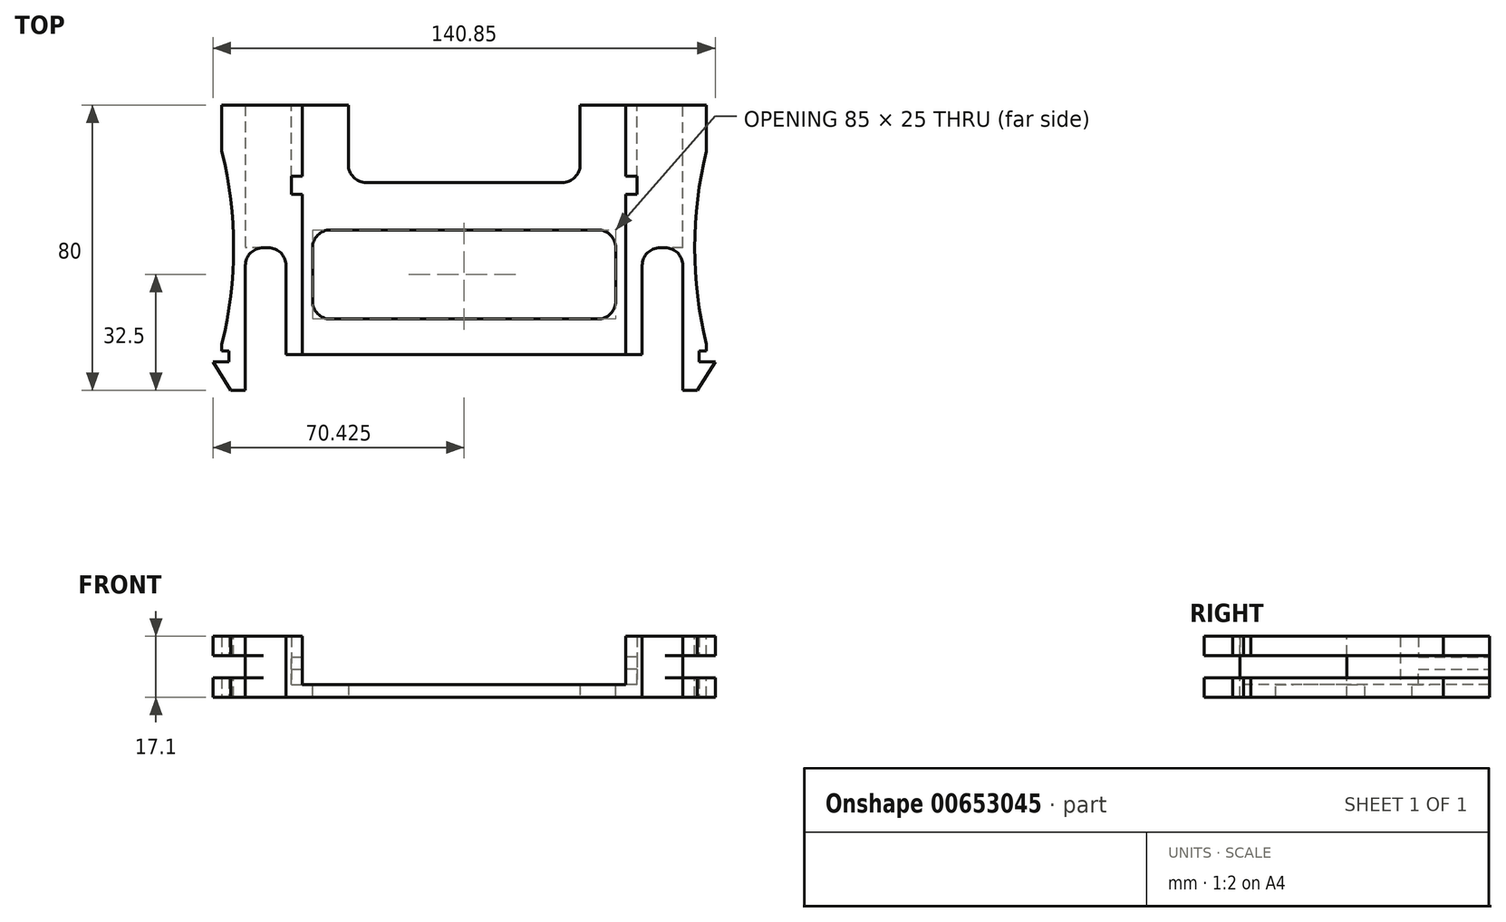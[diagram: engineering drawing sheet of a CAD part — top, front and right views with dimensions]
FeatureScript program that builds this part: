
annotation { "Feature Type Name" : "Feature", "Feature Type Description" : "" }
export const myFeature = defineFeature(function(context is Context, id is Id, definition is map)
    precondition{}
    {
        {
            var Q0;
            Q0=qCreatedBy(makeId("Top.planeOp"),FACE);
            var sketch = newSketch(context, id + "F0", { "sketchPlane" : qUnion([Q0])});
            skLineSegment(sketch, "E0.bottom", {"start": v(0, 0) * mm, "end": v(100.65, 0) * mm});
            skLineSegment(sketch, "E0.top", {"start": v(0, 134.5) * mm, "end": v(100.65, 134.5) * mm});
            skLineSegment(sketch, "E0.left", {"start": v(0, 0) * mm, "end": v(0, 134.5) * mm});
            skLineSegment(sketch, "E0.right", {"start": v(100.65, 0) * mm, "end": v(100.65, 134.5) * mm});
            skSolve(sketch);
        }
        {
            var Q0;
            Q0=makeQuery(id+"F0.imprint","IMPRINT",FACE,{"disambiguationData":[TD([[makeQuery(id+"F0.imprint","IMPRINT",EDGE,{"derivedFrom":sQuery(id+"F0.wireOp",EDGE,"E0.bottom")}),1.0]])]});
            extrude(context, id + "F1", {"entities" : qUnion([Q0]), "depth" : 2 * mm, "offsetDistance" : 25 * mm});
        }
        {
            var Q0;
            Q0=makeQuery(id+"F1.opExtrude","CAP_FACE",FACE,{"disambiguationData":[OSD([sQuery(id+"F0.wireOp",EDGE,"E0.bottom"),sQuery(id+"F0.wireOp",EDGE,"E0.top"),sQuery(id+"F0.wireOp",EDGE,"E0.left"),sQuery(id+"F0.wireOp",EDGE,"E0.right")])],"isStart":false});
            var sketch = newSketch(context, id + "F2", { "sketchPlane" : qUnion([Q0])});
            skLineSegment(sketch, "E1.bottom", {"start": v(0, 134.5) * mm, "end": v(5, 134.5) * mm});
            skLineSegment(sketch, "E1.top", {"start": v(0, 0) * mm, "end": v(5, 0) * mm});
            skLineSegment(sketch, "E1.left", {"start": v(0, 134.5) * mm, "end": v(0, 0) * mm});
            skLineSegment(sketch, "E1.right", {"start": v(5, 134.5) * mm, "end": v(5, 0) * mm});
            skLineSegment(sketch, "E2.bottom", {"start": v(100.65, 134.5) * mm, "end": v(95.65, 134.5) * mm});
            skLineSegment(sketch, "E2.top", {"start": v(100.65, 0) * mm, "end": v(95.65, 0) * mm});
            skLineSegment(sketch, "E2.left", {"start": v(100.65, 134.5) * mm, "end": v(100.65, 0) * mm});
            skLineSegment(sketch, "E2.right", {"start": v(95.65, 134.5) * mm, "end": v(95.65, 0) * mm});
            skSolve(sketch);
        }
        {
            var Q0;
            Q0=makeQuery(id+"F2.imprint","IMPRINT",FACE,{"disambiguationData":[TD([[makeQuery(id+"F2.imprint","IMPRINT",EDGE,{"derivedFrom":sQuery(id+"F2.wireOp",EDGE,"E1.bottom")}),-1.0]])]});
            var Q1;
            Q1=makeQuery(id+"F2.imprint","IMPRINT",FACE,{"disambiguationData":[TD([[makeQuery(id+"F2.imprint","IMPRINT",EDGE,{"derivedFrom":sQuery(id+"F2.wireOp",EDGE,"E2.bottom")}),-1.0]])]});
            extrude(context, id + "F3", {"entities" : qUnion([Q0, Q1]), "operationType" : NewBodyOperationType.ADD, "depth" : 11.9 * mm, "offsetDistance" : 25 * mm});
        }
        {
            var Q0;
            Q0=makeQuery(id+"F3.boolean.opBoolean","MERGE",FACE,{"derivedFrom":[makeQuery(id+"F1.opExtrude","SWEPT_FACE",FACE,{"disambiguationData":[OSD([sQuery(id+"F0.wireOp",EDGE,"E0.top")])]}),makeQuery(id+"F3.opExtrude","SWEPT_FACE",FACE,{"disambiguationData":[OSD([sQuery(id+"F2.wireOp",EDGE,"E1.bottom")])]}),makeQuery(id+"F3.opExtrude","SWEPT_FACE",FACE,{"disambiguationData":[OSD([sQuery(id+"F2.wireOp",EDGE,"E2.bottom")])]})]});
            var sketch = newSketch(context, id + "F4", { "sketchPlane" : qUnion([Q0])});
            skLineSegment(sketch, "E3.bottom", {"start": v(-100.65, 13.9) * mm, "end": v(-95.65, 13.9) * mm});
            skLineSegment(sketch, "E3.top", {"start": v(-100.65, 0) * mm, "end": v(-95.65, 0) * mm});
            skLineSegment(sketch, "E3.left", {"start": v(-100.65, 13.9) * mm, "end": v(-100.65, 0) * mm});
            skLineSegment(sketch, "E3.right", {"start": v(-95.65, 13.9) * mm, "end": v(-95.65, 0) * mm});
            skLineSegment(sketch, "E4.bottom", {"start": v(0, 13.9) * mm, "end": v(-5, 13.9) * mm});
            skLineSegment(sketch, "E4.top", {"start": v(0, 0) * mm, "end": v(-5, 0) * mm});
            skLineSegment(sketch, "E4.left", {"start": v(0, 13.9) * mm, "end": v(0, 0) * mm});
            skLineSegment(sketch, "E4.right", {"start": v(-5, 13.9) * mm, "end": v(-5, 0) * mm});
            skSolve(sketch);
        }
        {
            var Q0;
            {var subQ1=sQuery(id+"F4.wireOp",EDGE,"E3.bottom");Q0=makeQuery(id+"F4.imprint","IMPRINT",FACE,{"disambiguationData":[TD([[makeQuery(id+"F4.imprint","IMPRINT",EDGE,{"derivedFrom":subQ1}),1.0]])]});}
            var Q1;
            {var subQ1=sQuery(id+"F4.wireOp",EDGE,"E4.bottom");Q1=makeQuery(id+"F4.imprint","IMPRINT",FACE,{"disambiguationData":[TD([[makeQuery(id+"F4.imprint","IMPRINT",EDGE,{"derivedFrom":subQ1}),1.0]])]});}
            extrude(context, id + "F5", {"entities" : qUnion([Q0, Q1]), "operationType" : NewBodyOperationType.ADD, "depth" : 45 * mm, "offsetDistance" : 25 * mm});
        }
        {
            var Q0;
            Q0=makeQuery(id+"F5.boolean.opBoolean","MERGE",FACE,{"derivedFrom":[makeQuery(id+"F3.opExtrude","SWEPT_FACE",FACE,{"disambiguationData":[OSD([sQuery(id+"F2.wireOp",EDGE,"E1.right")])]}),makeQuery(id+"F5.opExtrude","SWEPT_FACE",FACE,{"disambiguationData":[OSD([sQuery(id+"F4.wireOp",EDGE,"E4.right")])]})]});
            var sketch = newSketch(context, id + "F6", { "sketchPlane" : qUnion([Q0])});
            skLineSegment(sketch, "E5", {"start": v(45, 13.9) * mm, "end": v(45, 2) * mm});
            skLineSegment(sketch, "E6", {"start": v(134.5, 2) * mm, "end": v(134.5, 4.2) * mm});
            skLineSegment(sketch, "E7", {"start": v(50, 2) * mm, "end": v(50, 6.2) * mm});
            skLineSegment(sketch, "E8", {"start": v(50, 6.2) * mm, "end": v(70, 6.2) * mm});
            skLineSegment(sketch, "E9", {"start": v(70, 6.2) * mm, "end": v(134.5, 2) * mm});
            skLineSegment(sketch, "E10", {"start": v(134.5, 9.7) * mm, "end": v(179.5, 9.7) * mm});
            skLineSegment(sketch, "E11", {"start": v(134.5, 4.2) * mm, "end": v(179.5, 4.2) * mm});
            skLineSegment(sketch, "E12.trimOffspring", {"start": v(134.5, 9.7) * mm, "end": v(134.5, 13.9) * mm});
            skLineSegment(sketch, "E13", {"start": v(50, 13.9) * mm, "end": v(50, 9.7) * mm});
            skLineSegment(sketch, "E14", {"start": v(50, 9.7) * mm, "end": v(70, 9.7) * mm});
            skLineSegment(sketch, "E15", {"start": v(70, 9.7) * mm, "end": v(70, 13.9) * mm});
            skSolve(sketch);
        }
        {
            var Q0;
            Q0=makeQuery(id+"F5.boolean.opBoolean","MERGE",FACE,{"derivedFrom":[makeQuery(id+"F3.opExtrude","SWEPT_FACE",FACE,{"disambiguationData":[OSD([sQuery(id+"F2.wireOp",EDGE,"E2.right")])]}),makeQuery(id+"F5.opExtrude","SWEPT_FACE",FACE,{"disambiguationData":[OSD([sQuery(id+"F4.wireOp",EDGE,"E3.right")])]})]});
            var sketch = newSketch(context, id + "F7", { "sketchPlane" : qUnion([Q0])});
            skLineSegment(sketch, "E16", {"start": v(-45, 13.9) * mm, "end": v(-45, 2) * mm});
            skLineSegment(sketch, "E17", {"start": v(-134.5, 13.9) * mm, "end": v(-134.5, 9.7) * mm});
            skLineSegment(sketch, "E18", {"start": v(-50, 2) * mm, "end": v(-50, 6.2) * mm});
            skLineSegment(sketch, "E19", {"start": v(-50, 6.2) * mm, "end": v(-70, 6.2) * mm});
            skLineSegment(sketch, "E20", {"start": v(-70, 6.2) * mm, "end": v(-134.5, 2) * mm});
            skLineSegment(sketch, "E21", {"start": v(-179.5, 4.2) * mm, "end": v(-134.5, 4.2) * mm});
            skLineSegment(sketch, "E22", {"start": v(-179.5, 9.7) * mm, "end": v(-134.5, 9.7) * mm});
            skLineSegment(sketch, "E23.trimOffspring", {"start": v(-134.5, 4.2) * mm, "end": v(-134.5, 2) * mm});
            skLineSegment(sketch, "E24", {"start": v(-50, 13.9) * mm, "end": v(-50, 9.7) * mm});
            skLineSegment(sketch, "E25", {"start": v(-50, 9.7) * mm, "end": v(-70, 9.7) * mm});
            skLineSegment(sketch, "E26", {"start": v(-70, 9.7) * mm, "end": v(-70, 13.9) * mm});
            skSolve(sketch);
        }
        {
            var Q0;
            {var subQ0=sQuery(id+"F7.wireOp",EDGE,"E16");Q0=makeQuery(id+"F7.imprint","IMPRINT",FACE,{"disambiguationData":[TD([[makeQuery(id+"F7.imprint","IMPRINT",EDGE,{"derivedFrom":subQ0}),-1.0]])]});}
            extrude(context, id + "F8", {"entities" : qUnion([Q0]), "operationType" : NewBodyOperationType.REMOVE, "oppositeDirection" : true, "depth" : 3.1 * mm, "offsetDistance" : 25 * mm});
        }
        {
            var Q0;
            {var subQ3=sQuery(id+"F6.wireOp",EDGE,"E5");Q0=makeQuery(id+"F6.imprint","IMPRINT",FACE,{"disambiguationData":[TD([[makeQuery(id+"F6.imprint","IMPRINT",EDGE,{"derivedFrom":subQ3}),1.0]])]});}
            extrude(context, id + "F9", {"entities" : qUnion([Q0]), "operationType" : NewBodyOperationType.REMOVE, "oppositeDirection" : true, "depth" : 3.1 * mm, "offsetDistance" : 25 * mm});
        }
        {
            var Q0;
            Q0=makeQuery(id+"F9.boolean.opBoolean","MERGE",FACE,{"derivedFrom":[makeQuery(id+"F8.boolean.opBoolean","MERGE",FACE,{"derivedFrom":[makeQuery(id+"F1.opExtrude","CAP_FACE",FACE,{"disambiguationData":[OSD([sQuery(id+"F0.wireOp",EDGE,"E0.bottom"),sQuery(id+"F0.wireOp",EDGE,"E0.top"),sQuery(id+"F0.wireOp",EDGE,"E0.left"),sQuery(id+"F0.wireOp",EDGE,"E0.right")])],"isStart":false}),makeQuery(id+"F8.opExtrude","SWEPT_FACE",FACE,{"disambiguationData":[OSD([sQuery(id+"F2.wireOp",EDGE,"E2.right")])]})]}),makeQuery(id+"F9.opExtrude","SWEPT_FACE",FACE,{"disambiguationData":[OSD([sQuery(id+"F2.wireOp",EDGE,"E1.right")])]})]});
            var sketch = newSketch(context, id + "F10", { "sketchPlane" : qUnion([Q0])});
            skLineSegment(sketch, "E27.bottom", {"start": v(12.83, 35) * mm, "end": v(87.82, 35) * mm});
            skLineSegment(sketch, "E27.top", {"start": v(12.83, 10) * mm, "end": v(87.82, 10) * mm});
            skLineSegment(sketch, "E27.left", {"start": v(7.83, 30) * mm, "end": v(7.83, 15) * mm});
            skLineSegment(sketch, "E27.right", {"start": v(92.83, 30) * mm, "end": v(92.83, 15) * mm});
            skLineSegment(sketch, "E28.bottom", {"start": v(22.85, 83.32) * mm, "end": v(77.85, 83.32) * mm});
            skLineSegment(sketch, "E28.top", {"start": v(22.85, 48.32) * mm, "end": v(77.85, 48.32) * mm});
            skLineSegment(sketch, "E28.left", {"start": v(17.85, 78.32) * mm, "end": v(17.85, 53.32) * mm});
            skLineSegment(sketch, "E28.right", {"start": v(82.85, 78.32) * mm, "end": v(82.85, 53.32) * mm});
            skLineSegment(sketch, "E29.bottom", {"start": v(22.85, 127.47) * mm, "end": v(77.85, 127.47) * mm});
            skLineSegment(sketch, "E29.top", {"start": v(22.85, 92.47) * mm, "end": v(77.85, 92.47) * mm});
            skLineSegment(sketch, "E29.left", {"start": v(17.85, 122.47) * mm, "end": v(17.85, 97.47) * mm});
            skLineSegment(sketch, "E29.right", {"start": v(82.85, 122.47) * mm, "end": v(82.85, 97.47) * mm});
            skPoint(sketch, "E30.visualSharp", {"position": v(17.85, 127.47) * mm});
            skArc(sketch, "E30.filletArc", {"start": v(22.85, 127.47) * mm, "mid": v(19.31, 126) * mm, "end": v(17.85, 122.47) * mm});
            skPoint(sketch, "E31.visualSharp", {"position": v(82.85, 127.47) * mm});
            skArc(sketch, "E31.filletArc", {"start": v(82.85, 122.47) * mm, "mid": v(81.39, 126) * mm, "end": v(77.85, 127.47) * mm});
            skPoint(sketch, "E32.visualSharp", {"position": v(82.85, 92.47) * mm});
            skArc(sketch, "E32.filletArc", {"start": v(77.85, 92.47) * mm, "mid": v(81.39, 93.93) * mm, "end": v(82.85, 97.47) * mm});
            skPoint(sketch, "E33.visualSharp", {"position": v(17.85, 92.47) * mm});
            skArc(sketch, "E33.filletArc", {"start": v(17.85, 97.47) * mm, "mid": v(19.31, 93.93) * mm, "end": v(22.85, 92.47) * mm});
            skPoint(sketch, "E34.visualSharp", {"position": v(17.85, 83.32) * mm});
            skArc(sketch, "E34.filletArc", {"start": v(22.85, 83.32) * mm, "mid": v(19.31, 81.85) * mm, "end": v(17.85, 78.32) * mm});
            skPoint(sketch, "E35.visualSharp", {"position": v(82.85, 83.32) * mm});
            skArc(sketch, "E35.filletArc", {"start": v(82.85, 78.32) * mm, "mid": v(81.39, 81.85) * mm, "end": v(77.85, 83.32) * mm});
            skPoint(sketch, "E36.visualSharp", {"position": v(82.85, 48.32) * mm});
            skArc(sketch, "E36.filletArc", {"start": v(77.85, 48.32) * mm, "mid": v(81.39, 49.78) * mm, "end": v(82.85, 53.32) * mm});
            skPoint(sketch, "E37.visualSharp", {"position": v(17.85, 48.32) * mm});
            skArc(sketch, "E37.filletArc", {"start": v(17.85, 53.32) * mm, "mid": v(19.31, 49.78) * mm, "end": v(22.85, 48.32) * mm});
            skPoint(sketch, "E38.visualSharp", {"position": v(7.83, 35) * mm});
            skArc(sketch, "E38.filletArc", {"start": v(12.83, 35) * mm, "mid": v(9.29, 33.54) * mm, "end": v(7.83, 30) * mm});
            skPoint(sketch, "E39.visualSharp", {"position": v(92.83, 35) * mm});
            skArc(sketch, "E39.filletArc", {"start": v(92.83, 30) * mm, "mid": v(91.36, 33.54) * mm, "end": v(87.82, 35) * mm});
            skPoint(sketch, "E40.visualSharp", {"position": v(92.83, 10) * mm});
            skArc(sketch, "E40.filletArc", {"start": v(87.82, 10) * mm, "mid": v(91.36, 11.46) * mm, "end": v(92.83, 15) * mm});
            skPoint(sketch, "E41.visualSharp", {"position": v(7.83, 10) * mm});
            skArc(sketch, "E41.filletArc", {"start": v(7.83, 15) * mm, "mid": v(9.29, 11.46) * mm, "end": v(12.83, 10) * mm});
            skSolve(sketch);
        }
        {
            var Q0;
            Q0=makeQuery(id+"F10.imprint","IMPRINT",FACE,{"disambiguationData":[TD([[makeQuery(id+"F10.imprint","IMPRINT",EDGE,{"derivedFrom":sQuery(id+"F10.wireOp",EDGE,"E29.bottom")}),-1.0]])]});
            var Q1;
            Q1=makeQuery(id+"F10.imprint","IMPRINT",FACE,{"disambiguationData":[TD([[makeQuery(id+"F10.imprint","IMPRINT",EDGE,{"derivedFrom":sQuery(id+"F10.wireOp",EDGE,"E28.bottom")}),-1.0]])]});
            var Q2;
            Q2=makeQuery(id+"F10.imprint","IMPRINT",FACE,{"disambiguationData":[TD([[makeQuery(id+"F10.imprint","IMPRINT",EDGE,{"derivedFrom":sQuery(id+"F10.wireOp",EDGE,"E27.bottom")}),-1.0]])]});
            extrude(context, id + "F11", {"entities" : qUnion([Q0, Q1, Q2]), "operationType" : NewBodyOperationType.REMOVE, "oppositeDirection" : true, "depth" : 2 * mm, "offsetDistance" : 25 * mm});
        }
        {
            var Q0;
            Q0=makeQuery(id+"F5.boolean.opBoolean","MERGE",FACE,{"derivedFrom":[makeQuery(id+"F3.opExtrude","CAP_FACE",FACE,{"disambiguationData":[OSD([sQuery(id+"F2.wireOp",EDGE,"E2.bottom"),sQuery(id+"F2.wireOp",EDGE,"E2.top"),sQuery(id+"F2.wireOp",EDGE,"E2.left"),sQuery(id+"F2.wireOp",EDGE,"E2.right")])],"isStart":false}),makeQuery(id+"F5.opExtrude","SWEPT_FACE",FACE,{"disambiguationData":[OSD([sQuery(id+"F4.wireOp",EDGE,"E3.bottom")])]})]});
            var Q1;
            Q1=makeQuery(id+"F5.boolean.opBoolean","MERGE",FACE,{"derivedFrom":[makeQuery(id+"F3.opExtrude","CAP_FACE",FACE,{"disambiguationData":[OSD([sQuery(id+"F2.wireOp",EDGE,"E1.bottom"),sQuery(id+"F2.wireOp",EDGE,"E1.top"),sQuery(id+"F2.wireOp",EDGE,"E1.left"),sQuery(id+"F2.wireOp",EDGE,"E1.right")])],"isStart":false}),makeQuery(id+"F5.opExtrude","SWEPT_FACE",FACE,{"disambiguationData":[OSD([sQuery(id+"F4.wireOp",EDGE,"E4.bottom")])]})]});
            extrude(context, id + "F12", {"entities" : qUnion([Q0, Q1]), "operationType" : NewBodyOperationType.ADD, "depth" : 1.6 * mm, "offsetDistance" : 25 * mm});
        }
        {
            var Q0;
            Q0=makeQuery(id+"F5.boolean.opBoolean","MERGE",FACE,{"derivedFrom":[makeQuery(id+"F1.opExtrude","CAP_FACE",FACE,{"disambiguationData":[OSD([sQuery(id+"F0.wireOp",EDGE,"E0.bottom"),sQuery(id+"F0.wireOp",EDGE,"E0.top"),sQuery(id+"F0.wireOp",EDGE,"E0.left"),sQuery(id+"F0.wireOp",EDGE,"E0.right")])],"isStart":true}),makeQuery(id+"F5.opExtrude","SWEPT_FACE",FACE,{"disambiguationData":[OSD([sQuery(id+"F4.wireOp",EDGE,"E3.top")])]}),makeQuery(id+"F5.opExtrude","SWEPT_FACE",FACE,{"disambiguationData":[OSD([sQuery(id+"F4.wireOp",EDGE,"E4.top")])]})]});
            extrude(context, id + "F13", {"entities" : qUnion([Q0]), "operationType" : NewBodyOperationType.ADD, "depth" : 1.6 * mm, "offsetDistance" : 25 * mm});
        }
        {
            var Q0;
            {var subQ0=sQuery(id+"F4.wireOp",EDGE,"E3.left");var subQ1=sQuery(id+"F0.wireOp",EDGE,"E0.right");var subQ2=sQuery(id+"F2.wireOp",EDGE,"E2.left");Q0=makeQuery(id+"F13.boolean.opBoolean","MERGE",FACE,{"derivedFrom":[makeQuery(id+"F12.boolean.opBoolean","MERGE",FACE,{"derivedFrom":[makeQuery(id+"F5.boolean.opBoolean","MERGE",FACE,{"derivedFrom":[makeQuery(id+"F3.boolean.opBoolean","MERGE",FACE,{"derivedFrom":[makeQuery(id+"F1.opExtrude","SWEPT_FACE",FACE,{"disambiguationData":[OSD([subQ1])]}),makeQuery(id+"F3.opExtrude","SWEPT_FACE",FACE,{"disambiguationData":[OSD([subQ2])]})]}),makeQuery(id+"F5.opExtrude","SWEPT_FACE",FACE,{"disambiguationData":[OSD([subQ0])]})]}),makeQuery(id+"F12.opExtrude","SWEPT_FACE",FACE,{"disambiguationData":[OSD([subQ2,sQuery(id+"F4.wireOp",EDGE,"E3.bottom"),subQ0])]})]}),makeQuery(id+"F13.opExtrude","SWEPT_FACE",FACE,{"disambiguationData":[OSD([subQ1,sQuery(id+"F4.wireOp",EDGE,"E3.top"),subQ0])]})]});}
            extrude(context, id + "F14", {"entities" : qUnion([Q0]), "operationType" : NewBodyOperationType.ADD, "depth" : 17.6 * mm, "offsetDistance" : 25 * mm});
        }
        {
            var Q0;
            {var subQ0=sQuery(id+"F4.wireOp",EDGE,"E4.left");var subQ1=sQuery(id+"F0.wireOp",EDGE,"E0.left");var subQ2=sQuery(id+"F2.wireOp",EDGE,"E1.left");Q0=makeQuery(id+"F13.boolean.opBoolean","MERGE",FACE,{"derivedFrom":[makeQuery(id+"F12.boolean.opBoolean","MERGE",FACE,{"derivedFrom":[makeQuery(id+"F5.boolean.opBoolean","MERGE",FACE,{"derivedFrom":[makeQuery(id+"F3.boolean.opBoolean","MERGE",FACE,{"derivedFrom":[makeQuery(id+"F1.opExtrude","SWEPT_FACE",FACE,{"disambiguationData":[OSD([subQ1])]}),makeQuery(id+"F3.opExtrude","SWEPT_FACE",FACE,{"disambiguationData":[OSD([subQ2])]})]}),makeQuery(id+"F5.opExtrude","SWEPT_FACE",FACE,{"disambiguationData":[OSD([subQ0])]})]}),makeQuery(id+"F12.opExtrude","SWEPT_FACE",FACE,{"disambiguationData":[OSD([subQ2,sQuery(id+"F4.wireOp",EDGE,"E4.bottom"),subQ0])]})]}),makeQuery(id+"F13.opExtrude","SWEPT_FACE",FACE,{"disambiguationData":[OSD([subQ1,sQuery(id+"F4.wireOp",EDGE,"E4.top"),subQ0])]})]});}
            extrude(context, id + "F15", {"entities" : qUnion([Q0]), "operationType" : NewBodyOperationType.ADD, "depth" : 17.6 * mm, "offsetDistance" : 25 * mm});
        }
        {
            var Q0;
            Q0=makeQuery(id+"F14.opExtrude","CAP_FACE",FACE,{"disambiguationData":[OSD([sQuery(id+"F0.wireOp",EDGE,"E0.right"),sQuery(id+"F2.wireOp",EDGE,"E2.left"),sQuery(id+"F4.wireOp",EDGE,"E3.bottom"),sQuery(id+"F4.wireOp",EDGE,"E3.top"),sQuery(id+"F4.wireOp",EDGE,"E3.left")])],"isStart":false});
            var sketch = newSketch(context, id + "F16", { "sketchPlane" : qUnion([Q0])});
            skLineSegment(sketch, "E42", {"start": v(0, 3.85) * mm, "end": v(179.5, 3.85) * mm});
            skLineSegment(sketch, "E43", {"start": v(0, 10.05) * mm, "end": v(179.5, 10.05) * mm});
            skSolve(sketch);
        }
        {
            var Q0;
            {var subQ0=sQuery(id+"F16.wireOp",EDGE,"E42");Q0=makeQuery(id+"F16.imprint","IMPRINT",FACE,{"disambiguationData":[TD([[makeQuery(id+"F16.imprint","IMPRINT",EDGE,{"derivedFrom":subQ0}),1.0]])]});}
            extrude(context, id + "F17", {"entities" : qUnion([Q0]), "operationType" : NewBodyOperationType.REMOVE, "oppositeDirection" : true, "depth" : 6.6 * mm, "offsetDistance" : 25 * mm});
        }
        {
            var Q0;
            Q0=makeQuery(id+"F15.opExtrude","CAP_FACE",FACE,{"disambiguationData":[OSD([sQuery(id+"F0.wireOp",EDGE,"E0.left"),sQuery(id+"F2.wireOp",EDGE,"E1.left"),sQuery(id+"F4.wireOp",EDGE,"E4.bottom"),sQuery(id+"F4.wireOp",EDGE,"E4.top"),sQuery(id+"F4.wireOp",EDGE,"E4.left")])],"isStart":false});
            var sketch = newSketch(context, id + "F18", { "sketchPlane" : qUnion([Q0])});
            skLineSegment(sketch, "E44", {"start": v(-179.5, 10.05) * mm, "end": v(0, 10.05) * mm});
            skLineSegment(sketch, "E45", {"start": v(-179.5, 3.85) * mm, "end": v(0, 3.85) * mm});
            skSolve(sketch);
        }
        {
            var Q0;
            {var subQ0=sQuery(id+"F18.wireOp",EDGE,"E44");Q0=makeQuery(id+"F18.imprint","IMPRINT",FACE,{"disambiguationData":[TD([[makeQuery(id+"F18.imprint","IMPRINT",EDGE,{"derivedFrom":subQ0}),-1.0]])]});}
            extrude(context, id + "F19", {"entities" : qUnion([Q0]), "operationType" : NewBodyOperationType.REMOVE, "oppositeDirection" : true, "depth" : 6.6 * mm, "offsetDistance" : 25 * mm});
        }
        {
            var Q0;
            {var subQ0=sQuery(id+"F2.wireOp",EDGE,"E1.top");var subQ1=sQuery(id+"F0.wireOp",EDGE,"E0.bottom");var subQ2=sQuery(id+"F2.wireOp",EDGE,"E2.top");Q0=makeQuery(id+"F15.boolean.opBoolean","MERGE",FACE,{"derivedFrom":[makeQuery(id+"F14.boolean.opBoolean","MERGE",FACE,{"derivedFrom":[makeQuery(id+"F13.boolean.opBoolean","MERGE",FACE,{"derivedFrom":[makeQuery(id+"F12.boolean.opBoolean","MERGE",FACE,{"derivedFrom":[makeQuery(id+"F3.boolean.opBoolean","MERGE",FACE,{"derivedFrom":[makeQuery(id+"F1.opExtrude","SWEPT_FACE",FACE,{"disambiguationData":[OSD([subQ1])]}),makeQuery(id+"F3.opExtrude","SWEPT_FACE",FACE,{"disambiguationData":[OSD([subQ0])]}),makeQuery(id+"F3.opExtrude","SWEPT_FACE",FACE,{"disambiguationData":[OSD([subQ2])]})]}),makeQuery(id+"F12.opExtrude","SWEPT_FACE",FACE,{"disambiguationData":[OSD([subQ0])]}),makeQuery(id+"F12.opExtrude","SWEPT_FACE",FACE,{"disambiguationData":[OSD([subQ2])]})]}),makeQuery(id+"F13.opExtrude","SWEPT_FACE",FACE,{"disambiguationData":[OSD([subQ1])]})]}),makeQuery(id+"F14.opExtrude","SWEPT_FACE",FACE,{"disambiguationData":[OSD([subQ1,sQuery(id+"F0.wireOp",EDGE,"E0.right"),subQ2,sQuery(id+"F2.wireOp",EDGE,"E2.left")])]})]}),makeQuery(id+"F15.opExtrude","SWEPT_FACE",FACE,{"disambiguationData":[OSD([subQ1,sQuery(id+"F0.wireOp",EDGE,"E0.left"),subQ0,sQuery(id+"F2.wireOp",EDGE,"E1.left")])]})]});}
            var sketch = newSketch(context, id + "F20", { "sketchPlane" : qUnion([Q0])});
            skLineSegment(sketch, "E46", {"start": v(-11, -1.6) * mm, "end": v(-11, 15.5) * mm});
            skLineSegment(sketch, "E47", {"start": v(0.4, -1.6) * mm, "end": v(0.4, 15.5) * mm});
            skLineSegment(sketch, "E48", {"start": v(111.65, -1.6) * mm, "end": v(111.65, 15.5) * mm});
            skLineSegment(sketch, "E49", {"start": v(100.25, -1.6) * mm, "end": v(100.25, 15.5) * mm});
            skSolve(sketch);
        }
        {
            var Q0;
            {var subQ0=sQuery(id+"F20.wireOp",EDGE,"E49");Q0=makeQuery(id+"F20.imprint","IMPRINT",FACE,{"disambiguationData":[TD([[makeQuery(id+"F20.imprint","IMPRINT",EDGE,{"derivedFrom":subQ0}),-1.0]])]});}
            var Q1;
            {var subQ0=sQuery(id+"F20.wireOp",EDGE,"E47");Q1=makeQuery(id+"F20.imprint","IMPRINT",FACE,{"disambiguationData":[TD([[makeQuery(id+"F20.imprint","IMPRINT",EDGE,{"derivedFrom":subQ0}),1.0]])]});}
            extrude(context, id + "F21", {"entities" : qUnion([Q0, Q1]), "operationType" : NewBodyOperationType.REMOVE, "oppositeDirection" : true, "depth" : 30 * mm, "offsetDistance" : 25 * mm});
        }
        {
            var Q0;
            {var subQ2=sQuery(id+"F2.wireOp",EDGE,"E2.left");var subQ3=sQuery(id+"F0.wireOp",EDGE,"E0.right");var subQ4=sQuery(id+"F2.wireOp",EDGE,"E2.top");var subQ5=sQuery(id+"F2.wireOp",EDGE,"E1.top");var subQ6=sQuery(id+"F0.wireOp",EDGE,"E0.bottom");Q0=makeQuery(id+"F21.boolean.opBoolean","SPLIT",FACE,{"disambiguationData":[TD([makeQuery(id+"F17.boolean.opBoolean","COPY",FACE,{"derivedFrom":makeQuery(id+"F17.opExtrude","SWEPT_FACE",FACE,{"disambiguationData":[OSD([sQuery(id+"F16.wireOp",EDGE,"E43")])]})})])],"derivedFrom":makeQuery(id+"F15.boolean.opBoolean","MERGE",FACE,{"derivedFrom":[makeQuery(id+"F14.boolean.opBoolean","MERGE",FACE,{"derivedFrom":[makeQuery(id+"F13.boolean.opBoolean","MERGE",FACE,{"derivedFrom":[makeQuery(id+"F12.boolean.opBoolean","MERGE",FACE,{"derivedFrom":[makeQuery(id+"F3.boolean.opBoolean","MERGE",FACE,{"derivedFrom":[makeQuery(id+"F1.opExtrude","SWEPT_FACE",FACE,{"disambiguationData":[OSD([subQ6])]}),makeQuery(id+"F3.opExtrude","SWEPT_FACE",FACE,{"disambiguationData":[OSD([subQ5])]}),makeQuery(id+"F3.opExtrude","SWEPT_FACE",FACE,{"disambiguationData":[OSD([subQ4])]})]}),makeQuery(id+"F12.opExtrude","SWEPT_FACE",FACE,{"disambiguationData":[OSD([subQ5])]}),makeQuery(id+"F12.opExtrude","SWEPT_FACE",FACE,{"disambiguationData":[OSD([subQ4])]})]}),makeQuery(id+"F13.opExtrude","SWEPT_FACE",FACE,{"disambiguationData":[OSD([subQ6])]})]}),makeQuery(id+"F14.opExtrude","SWEPT_FACE",FACE,{"disambiguationData":[OSD([subQ6,subQ3,subQ4,subQ2])]})]}),makeQuery(id+"F15.opExtrude","SWEPT_FACE",FACE,{"disambiguationData":[OSD([subQ6,sQuery(id+"F0.wireOp",EDGE,"E0.left"),subQ5,sQuery(id+"F2.wireOp",EDGE,"E1.left")])]})]})});}
            var Q1;
            {var subQ1=sQuery(id+"F0.wireOp",EDGE,"E0.left");var subQ4=sQuery(id+"F2.wireOp",EDGE,"E2.left");var subQ5=sQuery(id+"F0.wireOp",EDGE,"E0.right");var subQ6=sQuery(id+"F0.wireOp",EDGE,"E0.bottom");var subQ7=sQuery(id+"F2.wireOp",EDGE,"E1.top");var subQ8=sQuery(id+"F2.wireOp",EDGE,"E2.top");Q1=makeQuery(id+"F21.boolean.opBoolean","SPLIT",FACE,{"disambiguationData":[TD([makeQuery(id+"F17.boolean.opBoolean","COPY",FACE,{"derivedFrom":makeQuery(id+"F17.opExtrude","SWEPT_FACE",FACE,{"disambiguationData":[OSD([sQuery(id+"F16.wireOp",EDGE,"E42")])]})})])],"derivedFrom":makeQuery(id+"F15.boolean.opBoolean","MERGE",FACE,{"derivedFrom":[makeQuery(id+"F14.boolean.opBoolean","MERGE",FACE,{"derivedFrom":[makeQuery(id+"F13.boolean.opBoolean","MERGE",FACE,{"derivedFrom":[makeQuery(id+"F12.boolean.opBoolean","MERGE",FACE,{"derivedFrom":[makeQuery(id+"F3.boolean.opBoolean","MERGE",FACE,{"derivedFrom":[makeQuery(id+"F1.opExtrude","SWEPT_FACE",FACE,{"disambiguationData":[OSD([subQ6])]}),makeQuery(id+"F3.opExtrude","SWEPT_FACE",FACE,{"disambiguationData":[OSD([subQ7])]}),makeQuery(id+"F3.opExtrude","SWEPT_FACE",FACE,{"disambiguationData":[OSD([subQ8])]})]}),makeQuery(id+"F12.opExtrude","SWEPT_FACE",FACE,{"disambiguationData":[OSD([subQ7])]}),makeQuery(id+"F12.opExtrude","SWEPT_FACE",FACE,{"disambiguationData":[OSD([subQ8])]})]}),makeQuery(id+"F13.opExtrude","SWEPT_FACE",FACE,{"disambiguationData":[OSD([subQ6])]})]}),makeQuery(id+"F14.opExtrude","SWEPT_FACE",FACE,{"disambiguationData":[OSD([subQ6,subQ5,subQ8,subQ4])]})]}),makeQuery(id+"F15.opExtrude","SWEPT_FACE",FACE,{"disambiguationData":[OSD([subQ6,subQ1,subQ7,sQuery(id+"F2.wireOp",EDGE,"E1.left")])]})]})});}
            var Q2;
            {var subQ1=sQuery(id+"F2.wireOp",EDGE,"E1.left");var subQ2=sQuery(id+"F2.wireOp",EDGE,"E1.top");var subQ4=sQuery(id+"F0.wireOp",EDGE,"E0.left");var subQ5=sQuery(id+"F0.wireOp",EDGE,"E0.bottom");var subQ6=sQuery(id+"F2.wireOp",EDGE,"E2.top");Q2=makeQuery(id+"F21.boolean.opBoolean","SPLIT",FACE,{"disambiguationData":[TD([makeQuery(id+"F19.boolean.opBoolean","COPY",FACE,{"derivedFrom":makeQuery(id+"F19.opExtrude","SWEPT_FACE",FACE,{"disambiguationData":[OSD([sQuery(id+"F18.wireOp",EDGE,"E44")])]})})])],"derivedFrom":makeQuery(id+"F15.boolean.opBoolean","MERGE",FACE,{"derivedFrom":[makeQuery(id+"F14.boolean.opBoolean","MERGE",FACE,{"derivedFrom":[makeQuery(id+"F13.boolean.opBoolean","MERGE",FACE,{"derivedFrom":[makeQuery(id+"F12.boolean.opBoolean","MERGE",FACE,{"derivedFrom":[makeQuery(id+"F3.boolean.opBoolean","MERGE",FACE,{"derivedFrom":[makeQuery(id+"F1.opExtrude","SWEPT_FACE",FACE,{"disambiguationData":[OSD([subQ5])]}),makeQuery(id+"F3.opExtrude","SWEPT_FACE",FACE,{"disambiguationData":[OSD([subQ2])]}),makeQuery(id+"F3.opExtrude","SWEPT_FACE",FACE,{"disambiguationData":[OSD([subQ6])]})]}),makeQuery(id+"F12.opExtrude","SWEPT_FACE",FACE,{"disambiguationData":[OSD([subQ2])]}),makeQuery(id+"F12.opExtrude","SWEPT_FACE",FACE,{"disambiguationData":[OSD([subQ6])]})]}),makeQuery(id+"F13.opExtrude","SWEPT_FACE",FACE,{"disambiguationData":[OSD([subQ5])]})]}),makeQuery(id+"F14.opExtrude","SWEPT_FACE",FACE,{"disambiguationData":[OSD([subQ5,sQuery(id+"F0.wireOp",EDGE,"E0.right"),subQ6,sQuery(id+"F2.wireOp",EDGE,"E2.left")])]})]}),makeQuery(id+"F15.opExtrude","SWEPT_FACE",FACE,{"disambiguationData":[OSD([subQ5,subQ4,subQ2,subQ1])]})]})});}
            var Q3;
            {var subQ2=sQuery(id+"F2.wireOp",EDGE,"E1.left");var subQ3=sQuery(id+"F0.wireOp",EDGE,"E0.left");var subQ5=sQuery(id+"F0.wireOp",EDGE,"E0.right");var subQ6=sQuery(id+"F0.wireOp",EDGE,"E0.bottom");var subQ7=sQuery(id+"F2.wireOp",EDGE,"E1.top");var subQ8=sQuery(id+"F2.wireOp",EDGE,"E2.top");Q3=makeQuery(id+"F21.boolean.opBoolean","SPLIT",FACE,{"disambiguationData":[TD([makeQuery(id+"F19.boolean.opBoolean","COPY",FACE,{"derivedFrom":makeQuery(id+"F19.opExtrude","SWEPT_FACE",FACE,{"disambiguationData":[OSD([sQuery(id+"F18.wireOp",EDGE,"E45")])]})})])],"derivedFrom":makeQuery(id+"F15.boolean.opBoolean","MERGE",FACE,{"derivedFrom":[makeQuery(id+"F14.boolean.opBoolean","MERGE",FACE,{"derivedFrom":[makeQuery(id+"F13.boolean.opBoolean","MERGE",FACE,{"derivedFrom":[makeQuery(id+"F12.boolean.opBoolean","MERGE",FACE,{"derivedFrom":[makeQuery(id+"F3.boolean.opBoolean","MERGE",FACE,{"derivedFrom":[makeQuery(id+"F1.opExtrude","SWEPT_FACE",FACE,{"disambiguationData":[OSD([subQ6])]}),makeQuery(id+"F3.opExtrude","SWEPT_FACE",FACE,{"disambiguationData":[OSD([subQ7])]}),makeQuery(id+"F3.opExtrude","SWEPT_FACE",FACE,{"disambiguationData":[OSD([subQ8])]})]}),makeQuery(id+"F12.opExtrude","SWEPT_FACE",FACE,{"disambiguationData":[OSD([subQ7])]}),makeQuery(id+"F12.opExtrude","SWEPT_FACE",FACE,{"disambiguationData":[OSD([subQ8])]})]}),makeQuery(id+"F13.opExtrude","SWEPT_FACE",FACE,{"disambiguationData":[OSD([subQ6])]})]}),makeQuery(id+"F14.opExtrude","SWEPT_FACE",FACE,{"disambiguationData":[OSD([subQ6,subQ5,subQ8,sQuery(id+"F2.wireOp",EDGE,"E2.left")])]})]}),makeQuery(id+"F15.opExtrude","SWEPT_FACE",FACE,{"disambiguationData":[OSD([subQ6,subQ3,subQ7,subQ2])]})]})});}
            extrude(context, id + "F22", {"entities" : qUnion([Q0, Q1, Q2, Q3]), "operationType" : NewBodyOperationType.ADD, "depth" : 10 * mm, "offsetDistance" : 25 * mm});
        }
        {
            var Q0;
            {var subQ0=sQuery(id+"F4.wireOp",EDGE,"E3.left");var subQ1=sQuery(id+"F4.wireOp",EDGE,"E3.top");var subQ2=sQuery(id+"F4.wireOp",EDGE,"E3.bottom");var subQ3=sQuery(id+"F2.wireOp",EDGE,"E2.left");var subQ4=sQuery(id+"F0.wireOp",EDGE,"E0.right");var subQ5=makeQuery(id+"F14.opExtrude","CAP_FACE",FACE,{"disambiguationData":[OSD([subQ4,subQ3,subQ2,subQ1,subQ0])],"isStart":false});var subQ6=sQuery(id+"F0.wireOp",EDGE,"E0.bottom");var subQ9=sQuery(id+"F2.wireOp",EDGE,"E2.top");var subQ14=makeQuery(id+"F17.opExtrude","SWEPT_FACE",FACE,{"disambiguationData":[OSD([sQuery(id+"F16.wireOp",EDGE,"E43")])]});Q0=makeQuery(id+"F22.boolean.opBoolean","MERGE",FACE,{"derivedFrom":[makeQuery(id+"F17.boolean.opBoolean","SPLIT",FACE,{"disambiguationData":[TD([subQ14])],"derivedFrom":subQ5}),makeQuery(id+"F22.opExtrude","SWEPT_FACE",FACE,{"disambiguationData":[OSD([subQ6,subQ4,subQ9,subQ3]),TDD([makeQuery(id+"F17.boolean.opBoolean","SPLIT",EDGE,{"disambiguationData":[TD([subQ14])],"derivedFrom":makeQuery(id+"F14.opExtrude","CAP_EDGE",EDGE,{"disambiguationData":[OSD([subQ6,subQ4,subQ9,subQ3])],"isStart":false})})])]})]});}
            var sketch = newSketch(context, id + "F23", { "sketchPlane" : qUnion([Q0])});
            skLineSegment(sketch, "E50", {"start": v(-2, 15.5) * mm, "end": v(-2, 10.05) * mm});
            skLineSegment(sketch, "E51", {"start": v(1, 15.5) * mm, "end": v(1, 10.05) * mm});
            skSolve(sketch);
        }
        {
            var Q0;
            {var subQ0=sQuery(id+"F4.wireOp",EDGE,"E3.left");var subQ1=sQuery(id+"F4.wireOp",EDGE,"E3.top");var subQ2=sQuery(id+"F4.wireOp",EDGE,"E3.bottom");var subQ3=sQuery(id+"F2.wireOp",EDGE,"E2.left");var subQ4=sQuery(id+"F0.wireOp",EDGE,"E0.right");var subQ5=makeQuery(id+"F14.opExtrude","CAP_FACE",FACE,{"disambiguationData":[OSD([subQ4,subQ3,subQ2,subQ1,subQ0])],"isStart":false});var subQ6=sQuery(id+"F0.wireOp",EDGE,"E0.bottom");var subQ9=sQuery(id+"F2.wireOp",EDGE,"E2.top");var subQ22=makeQuery(id+"F17.opExtrude","SWEPT_FACE",FACE,{"disambiguationData":[OSD([sQuery(id+"F16.wireOp",EDGE,"E42")])]});Q0=makeQuery(id+"F22.boolean.opBoolean","MERGE",FACE,{"derivedFrom":[makeQuery(id+"F17.boolean.opBoolean","SPLIT",FACE,{"disambiguationData":[TD([subQ22])],"derivedFrom":subQ5}),makeQuery(id+"F22.opExtrude","SWEPT_FACE",FACE,{"disambiguationData":[OSD([subQ6,subQ4,subQ9,subQ3]),TDD([makeQuery(id+"F17.boolean.opBoolean","SPLIT",EDGE,{"disambiguationData":[TD([subQ22])],"derivedFrom":makeQuery(id+"F14.opExtrude","CAP_EDGE",EDGE,{"disambiguationData":[OSD([subQ6,subQ4,subQ9,subQ3])],"isStart":false})})])]})]});}
            var sketch = newSketch(context, id + "F24", { "sketchPlane" : qUnion([Q0])});
            skLineSegment(sketch, "E52", {"start": v(-2, 3.85) * mm, "end": v(-2, -1.6) * mm});
            skLineSegment(sketch, "E53", {"start": v(1, 3.85) * mm, "end": v(1, -1.6) * mm});
            skSolve(sketch);
        }
        {
            var Q0;
            {var subQ0=sQuery(id+"F23.wireOp",EDGE,"E50");Q0=makeQuery(id+"F23.imprint","IMPRINT",FACE,{"disambiguationData":[TD([[makeQuery(id+"F23.imprint","IMPRINT",EDGE,{"derivedFrom":subQ0}),-1.0]])]});}
            var Q1;
            {var subQ0=sQuery(id+"F24.wireOp",EDGE,"E52");Q1=makeQuery(id+"F24.imprint","IMPRINT",FACE,{"disambiguationData":[TD([[makeQuery(id+"F24.imprint","IMPRINT",EDGE,{"derivedFrom":subQ0}),-1.0]])]});}
            extrude(context, id + "F25", {"entities" : qUnion([Q0, Q1]), "operationType" : NewBodyOperationType.ADD, "depth" : 5 * mm, "offsetDistance" : 25 * mm});
        }
        {
            var Q0;
            {var subQ0=sQuery(id+"F23.wireOp",EDGE,"E50");Q0=makeQuery(id+"F23.imprint","IMPRINT",FACE,{"disambiguationData":[TD([[makeQuery(id+"F23.imprint","IMPRINT",EDGE,{"derivedFrom":subQ0}),1.0]])]});}
            var Q1;
            {var subQ0=sQuery(id+"F24.wireOp",EDGE,"E52");Q1=makeQuery(id+"F24.imprint","IMPRINT",FACE,{"disambiguationData":[TD([[makeQuery(id+"F24.imprint","IMPRINT",EDGE,{"derivedFrom":subQ0}),1.0]])]});}
            extrude(context, id + "F26", {"entities" : qUnion([Q0, Q1]), "operationType" : NewBodyOperationType.REMOVE, "oppositeDirection" : true, "depth" : 2 * mm, "offsetDistance" : 25 * mm});
        }
        {
            var Q0;
            {var subQ0=sQuery(id+"F4.wireOp",EDGE,"E4.left");var subQ1=sQuery(id+"F4.wireOp",EDGE,"E4.bottom");var subQ2=sQuery(id+"F2.wireOp",EDGE,"E1.left");var subQ6=sQuery(id+"F0.wireOp",EDGE,"E0.bottom");var subQ8=sQuery(id+"F2.wireOp",EDGE,"E1.top");var subQ11=sQuery(id+"F0.wireOp",EDGE,"E0.left");var subQ17=sQuery(id+"F4.wireOp",EDGE,"E4.top");var subQ18=makeQuery(id+"F15.opExtrude","CAP_FACE",FACE,{"disambiguationData":[OSD([subQ11,subQ2,subQ1,subQ17,subQ0])],"isStart":false});var subQ19=makeQuery(id+"F19.opExtrude","SWEPT_FACE",FACE,{"disambiguationData":[OSD([sQuery(id+"F18.wireOp",EDGE,"E44")])]});Q0=makeQuery(id+"F22.boolean.opBoolean","MERGE",FACE,{"derivedFrom":[makeQuery(id+"F19.boolean.opBoolean","SPLIT",FACE,{"disambiguationData":[TD([subQ19])],"derivedFrom":subQ18}),makeQuery(id+"F22.opExtrude","SWEPT_FACE",FACE,{"disambiguationData":[OSD([subQ6,subQ11,subQ8,subQ2]),TDD([makeQuery(id+"F19.boolean.opBoolean","SPLIT",EDGE,{"disambiguationData":[TD([subQ19])],"derivedFrom":makeQuery(id+"F15.opExtrude","CAP_EDGE",EDGE,{"disambiguationData":[OSD([subQ6,subQ11,subQ8,subQ2])],"isStart":false})})])]})]});}
            var sketch = newSketch(context, id + "F27", { "sketchPlane" : qUnion([Q0])});
            skLineSegment(sketch, "E54", {"start": v(2, 15.5) * mm, "end": v(2, 10.05) * mm});
            skLineSegment(sketch, "E55", {"start": v(-1, 15.5) * mm, "end": v(-1, 10.05) * mm});
            skSolve(sketch);
        }
        {
            var Q0;
            {var subQ2=sQuery(id+"F0.wireOp",EDGE,"E0.bottom");var subQ6=makeQuery(id+"F19.opExtrude","SWEPT_FACE",FACE,{"disambiguationData":[OSD([sQuery(id+"F18.wireOp",EDGE,"E45")])]});var subQ10=sQuery(id+"F4.wireOp",EDGE,"E4.top");var subQ11=sQuery(id+"F0.wireOp",EDGE,"E0.left");var subQ13=sQuery(id+"F2.wireOp",EDGE,"E1.top");var subQ16=sQuery(id+"F4.wireOp",EDGE,"E4.left");var subQ19=sQuery(id+"F2.wireOp",EDGE,"E1.left");var subQ21=sQuery(id+"F4.wireOp",EDGE,"E4.bottom");var subQ22=makeQuery(id+"F15.opExtrude","CAP_FACE",FACE,{"disambiguationData":[OSD([subQ11,subQ19,subQ21,subQ10,subQ16])],"isStart":false});Q0=makeQuery(id+"F22.boolean.opBoolean","MERGE",FACE,{"derivedFrom":[makeQuery(id+"F19.boolean.opBoolean","SPLIT",FACE,{"disambiguationData":[TD([subQ6])],"derivedFrom":subQ22}),makeQuery(id+"F22.opExtrude","SWEPT_FACE",FACE,{"disambiguationData":[OSD([subQ2,subQ11,subQ13,subQ19]),TDD([makeQuery(id+"F19.boolean.opBoolean","SPLIT",EDGE,{"disambiguationData":[TD([subQ6])],"derivedFrom":makeQuery(id+"F15.opExtrude","CAP_EDGE",EDGE,{"disambiguationData":[OSD([subQ2,subQ11,subQ13,subQ19])],"isStart":false})})])]})]});}
            var sketch = newSketch(context, id + "F28", { "sketchPlane" : qUnion([Q0])});
            skLineSegment(sketch, "E56", {"start": v(2, 3.85) * mm, "end": v(2, -1.6) * mm});
            skLineSegment(sketch, "E57", {"start": v(-1, 3.85) * mm, "end": v(-1, -1.6) * mm});
            skSolve(sketch);
        }
        {
            var Q0;
            {var subQ0=sQuery(id+"F27.wireOp",EDGE,"E54");Q0=makeQuery(id+"F27.imprint","IMPRINT",FACE,{"disambiguationData":[TD([[makeQuery(id+"F27.imprint","IMPRINT",EDGE,{"derivedFrom":subQ0}),1.0]])]});}
            var Q1;
            {var subQ0=sQuery(id+"F28.wireOp",EDGE,"E56");Q1=makeQuery(id+"F28.imprint","IMPRINT",FACE,{"disambiguationData":[TD([[makeQuery(id+"F28.imprint","IMPRINT",EDGE,{"derivedFrom":subQ0}),1.0]])]});}
            extrude(context, id + "F29", {"entities" : qUnion([Q0, Q1]), "operationType" : NewBodyOperationType.ADD, "depth" : 5 * mm, "offsetDistance" : 25 * mm});
        }
        {
            var Q0;
            {var subQ0=sQuery(id+"F27.wireOp",EDGE,"E54");Q0=makeQuery(id+"F27.imprint","IMPRINT",FACE,{"disambiguationData":[TD([[makeQuery(id+"F27.imprint","IMPRINT",EDGE,{"derivedFrom":subQ0}),-1.0]])]});}
            var Q1;
            {var subQ0=sQuery(id+"F28.wireOp",EDGE,"E56");Q1=makeQuery(id+"F28.imprint","IMPRINT",FACE,{"disambiguationData":[TD([[makeQuery(id+"F28.imprint","IMPRINT",EDGE,{"derivedFrom":subQ0}),-1.0]])]});}
            extrude(context, id + "F30", {"entities" : qUnion([Q0, Q1]), "operationType" : NewBodyOperationType.REMOVE, "oppositeDirection" : true, "depth" : 2 * mm, "offsetDistance" : 25 * mm});
        }
        {
            var Q0;
            {var subQ2=sQuery(id+"F2.wireOp",EDGE,"E2.left");var subQ3=sQuery(id+"F0.wireOp",EDGE,"E0.right");var subQ4=sQuery(id+"F0.wireOp",EDGE,"E0.bottom");var subQ5=sQuery(id+"F2.wireOp",EDGE,"E2.top");Q0=makeQuery(id+"F25.opExtrude","CAP_EDGE",EDGE,{"disambiguationData":[OSD([subQ4,subQ3,subQ5,subQ2]),TDD([makeQuery(id+"F24.imprint","IMPRINT",EDGE,{"derivedFrom":makeQuery(id+"F22.opExtrude","CAP_EDGE",EDGE,{"disambiguationData":[OSD([subQ4,subQ3,subQ5,subQ2]),TDD([makeQuery(id+"F17.boolean.opBoolean","SPLIT",EDGE,{"disambiguationData":[TD([makeQuery(id+"F17.opExtrude","SWEPT_FACE",FACE,{"disambiguationData":[OSD([sQuery(id+"F16.wireOp",EDGE,"E42")])]})])],"derivedFrom":makeQuery(id+"F14.opExtrude","CAP_EDGE",EDGE,{"disambiguationData":[OSD([subQ4,subQ3,subQ5,subQ2])],"isStart":false})})])],"isStart":false})})])],"isStart":false});}
            var Q1;
            {var subQ2=sQuery(id+"F2.wireOp",EDGE,"E2.left");var subQ3=sQuery(id+"F0.wireOp",EDGE,"E0.right");var subQ4=sQuery(id+"F0.wireOp",EDGE,"E0.bottom");var subQ5=sQuery(id+"F2.wireOp",EDGE,"E2.top");Q1=makeQuery(id+"F25.opExtrude","CAP_EDGE",EDGE,{"disambiguationData":[OSD([subQ4,subQ3,subQ5,subQ2]),TDD([makeQuery(id+"F23.imprint","IMPRINT",EDGE,{"derivedFrom":makeQuery(id+"F22.opExtrude","CAP_EDGE",EDGE,{"disambiguationData":[OSD([subQ4,subQ3,subQ5,subQ2]),TDD([makeQuery(id+"F17.boolean.opBoolean","SPLIT",EDGE,{"disambiguationData":[TD([makeQuery(id+"F17.opExtrude","SWEPT_FACE",FACE,{"disambiguationData":[OSD([sQuery(id+"F16.wireOp",EDGE,"E43")])]})])],"derivedFrom":makeQuery(id+"F14.opExtrude","CAP_EDGE",EDGE,{"disambiguationData":[OSD([subQ4,subQ3,subQ5,subQ2])],"isStart":false})})])],"isStart":false})})])],"isStart":false});}
            chamfer(context, id + "F31", {"entities" : qUnion([Q0, Q1]), "chamferType" : ChamferType.TWO_OFFSETS, "width1" : 8 * mm, "oppositeDirection" : false, "width2" : 5 * mm, "tangentPropagation" : true});
        }
        {
            var Q0;
            {var subQ2=sQuery(id+"F2.wireOp",EDGE,"E1.left");var subQ4=sQuery(id+"F0.wireOp",EDGE,"E0.bottom");var subQ5=sQuery(id+"F2.wireOp",EDGE,"E1.top");var subQ6=sQuery(id+"F0.wireOp",EDGE,"E0.left");Q0=makeQuery(id+"F29.opExtrude","CAP_EDGE",EDGE,{"disambiguationData":[OSD([subQ4,subQ6,subQ5,subQ2]),TDD([makeQuery(id+"F27.imprint","IMPRINT",EDGE,{"derivedFrom":makeQuery(id+"F22.opExtrude","CAP_EDGE",EDGE,{"disambiguationData":[OSD([subQ4,subQ6,subQ5,subQ2]),TDD([makeQuery(id+"F19.boolean.opBoolean","SPLIT",EDGE,{"disambiguationData":[TD([makeQuery(id+"F19.opExtrude","SWEPT_FACE",FACE,{"disambiguationData":[OSD([sQuery(id+"F18.wireOp",EDGE,"E44")])]})])],"derivedFrom":makeQuery(id+"F15.opExtrude","CAP_EDGE",EDGE,{"disambiguationData":[OSD([subQ4,subQ6,subQ5,subQ2])],"isStart":false})})])],"isStart":false})})])],"isStart":false});}
            var Q1;
            {var subQ2=sQuery(id+"F0.wireOp",EDGE,"E0.bottom");var subQ5=sQuery(id+"F0.wireOp",EDGE,"E0.left");var subQ6=sQuery(id+"F2.wireOp",EDGE,"E1.top");var subQ8=sQuery(id+"F2.wireOp",EDGE,"E1.left");Q1=makeQuery(id+"F29.opExtrude","CAP_EDGE",EDGE,{"disambiguationData":[OSD([subQ2,subQ5,subQ6,subQ8]),TDD([makeQuery(id+"F28.imprint","IMPRINT",EDGE,{"derivedFrom":makeQuery(id+"F22.opExtrude","CAP_EDGE",EDGE,{"disambiguationData":[OSD([subQ2,subQ5,subQ6,subQ8]),TDD([makeQuery(id+"F19.boolean.opBoolean","SPLIT",EDGE,{"disambiguationData":[TD([makeQuery(id+"F19.opExtrude","SWEPT_FACE",FACE,{"disambiguationData":[OSD([sQuery(id+"F18.wireOp",EDGE,"E45")])]})])],"derivedFrom":makeQuery(id+"F15.opExtrude","CAP_EDGE",EDGE,{"disambiguationData":[OSD([subQ2,subQ5,subQ6,subQ8])],"isStart":false})})])],"isStart":false})})])],"isStart":false});}
            chamfer(context, id + "F32", {"entities" : qUnion([Q0, Q1]), "chamferType" : ChamferType.TWO_OFFSETS, "width1" : 5 * mm, "oppositeDirection" : false, "width2" : 8 * mm, "tangentPropagation" : true});
        }
        {
            var Q0;
            {var subQ0=sQuery(id+"F4.wireOp",EDGE,"E4.left");var subQ1=sQuery(id+"F4.wireOp",EDGE,"E4.bottom");var subQ2=sQuery(id+"F2.wireOp",EDGE,"E1.left");var subQ3=sQuery(id+"F2.wireOp",EDGE,"E1.top");Q0=makeQuery(id+"F29.boolean.opBoolean","MERGE",FACE,{"derivedFrom":[makeQuery(id+"F22.boolean.opBoolean","MERGE",FACE,{"derivedFrom":[makeQuery(id+"F15.boolean.opBoolean","MERGE",FACE,{"derivedFrom":[makeQuery(id+"F12.opExtrude","CAP_FACE",FACE,{"disambiguationData":[OSD([sQuery(id+"F2.wireOp",EDGE,"E1.bottom"),subQ3,subQ2,sQuery(id+"F2.wireOp",EDGE,"E1.right"),subQ1])],"isStart":false}),makeQuery(id+"F15.opExtrude","SWEPT_FACE",FACE,{"disambiguationData":[OSD([subQ2,subQ1,subQ0])]})]}),makeQuery(id+"F22.opExtrude","SWEPT_FACE",FACE,{"disambiguationData":[OSD([subQ3,subQ2])]})]}),makeQuery(id+"F29.opExtrude","SWEPT_FACE",FACE,{"disambiguationData":[OSD([subQ3,subQ2,subQ1,subQ0])]})]});}
            var sketch = newSketch(context, id + "F33", { "sketchPlane" : qUnion([Q0])});
            skLineSegment(sketch, "E58", {"start": v(-15.1, -10) * mm, "end": v(-20.1, -2) * mm});
            skPoint(sketch, "E58.endSnap0", {"position": v(-20.1, -6) * mm});
            skLineSegment(sketch, "E59", {"start": v(-6.3, 179.5) * mm, "end": v(-6.3, 134.5) * mm});
            skPoint(sketch, "E59.endSnap0", {"position": v(3.45, 134.5) * mm});
            skLineSegment(sketch, "E60", {"start": v(-6.3, 134.5) * mm, "end": v(-17.6, 134.5) * mm});
            skArc(sketch, "E61", {"start": v(-17.6, 3) * mm, "mid": v(-14.3, 30) * mm, "end": v(-17.6, 57) * mm});
            skSolve(sketch);
        }
        {
            var Q0;
            {var subQ0=sQuery(id+"F33.wireOp",EDGE,"E58");Q0=makeQuery(id+"F33.imprint","IMPRINT",FACE,{"disambiguationData":[TD([[makeQuery(id+"F33.imprint","IMPRINT",EDGE,{"derivedFrom":subQ0}),1.0]])]});}
            var Q1;
            {var subQ0=sQuery(id+"F33.wireOp",EDGE,"XLUjgDC1-YMsP-lwaJ-gL8n-WkmhW8InEvri");Q1=makeQuery(id+"F33.imprint","IMPRINT",FACE,{"disambiguationData":[TD([[makeQuery(id+"F33.imprint","IMPRINT",EDGE,{"derivedFrom":subQ0}),1.0]])]});}
            var Q2;
            {var subQ0=sQuery(id+"F33.wireOp",EDGE,"E59");Q2=makeQuery(id+"F33.imprint","IMPRINT",FACE,{"disambiguationData":[TD([[makeQuery(id+"F33.imprint","IMPRINT",EDGE,{"derivedFrom":subQ0}),-1.0]])]});}
            var Q3;
            {var subQ0=sQuery(id+"F33.wireOp",EDGE,"E61");Q3=makeQuery(id+"F33.imprint","IMPRINT",FACE,{"disambiguationData":[TD([[makeQuery(id+"F33.imprint","IMPRINT",EDGE,{"derivedFrom":subQ0}),1.0]])]});}
            extrude(context, id + "F34", {"entities" : qUnion([Q0, Q1, Q2, Q3]), "operationType" : NewBodyOperationType.REMOVE, "oppositeDirection" : true, "depth" : 25 * mm, "offsetDistance" : 25 * mm});
        }
        {
            var Q0;
            {var subQ0=sQuery(id+"F4.wireOp",EDGE,"E3.left");var subQ1=sQuery(id+"F4.wireOp",EDGE,"E3.bottom");var subQ2=sQuery(id+"F2.wireOp",EDGE,"E2.left");var subQ3=sQuery(id+"F2.wireOp",EDGE,"E2.top");Q0=makeQuery(id+"F25.boolean.opBoolean","MERGE",FACE,{"derivedFrom":[makeQuery(id+"F22.boolean.opBoolean","MERGE",FACE,{"derivedFrom":[makeQuery(id+"F14.boolean.opBoolean","MERGE",FACE,{"derivedFrom":[makeQuery(id+"F12.opExtrude","CAP_FACE",FACE,{"disambiguationData":[OSD([sQuery(id+"F2.wireOp",EDGE,"E2.bottom"),subQ3,subQ2,sQuery(id+"F2.wireOp",EDGE,"E2.right"),subQ1])],"isStart":false}),makeQuery(id+"F14.opExtrude","SWEPT_FACE",FACE,{"disambiguationData":[OSD([subQ2,subQ1,subQ0])]})]}),makeQuery(id+"F22.opExtrude","SWEPT_FACE",FACE,{"disambiguationData":[OSD([subQ3,subQ2])]})]}),makeQuery(id+"F25.opExtrude","SWEPT_FACE",FACE,{"disambiguationData":[OSD([subQ3,subQ2,subQ1,subQ0])]})]});}
            var sketch = newSketch(context, id + "F35", { "sketchPlane" : qUnion([Q0])});
            skLineSegment(sketch, "E62", {"start": v(120.75, -2) * mm, "end": v(115.75, -10) * mm});
            skPoint(sketch, "E62.startSnap0", {"position": v(120.75, -6) * mm});
            skLineSegment(sketch, "E63", {"start": v(106.95, 179.5) * mm, "end": v(106.95, 134.5) * mm});
            skLineSegment(sketch, "E64", {"start": v(106.95, 134.5) * mm, "end": v(118.25, 134.5) * mm});
            skArc(sketch, "E65", {"start": v(118.25, 57) * mm, "mid": v(114.95, 30) * mm, "end": v(118.25, 3) * mm});
            skSolve(sketch);
        }
        {
            var Q0;
            {var subQ0=sQuery(id+"F35.wireOp",EDGE,"ahOdGnL4-bCum-fQt1-Ztqo-JPbCzPc07AA6");Q0=makeQuery(id+"F35.imprint","IMPRINT",FACE,{"disambiguationData":[TD([[makeQuery(id+"F35.imprint","IMPRINT",EDGE,{"derivedFrom":subQ0}),1.0]])]});}
            var Q1;
            {var subQ0=sQuery(id+"F35.wireOp",EDGE,"E62");Q1=makeQuery(id+"F35.imprint","IMPRINT",FACE,{"disambiguationData":[TD([[makeQuery(id+"F35.imprint","IMPRINT",EDGE,{"derivedFrom":subQ0}),1.0]])]});}
            var Q2;
            {var subQ0=sQuery(id+"F35.wireOp",EDGE,"E63");Q2=makeQuery(id+"F35.imprint","IMPRINT",FACE,{"disambiguationData":[TD([[makeQuery(id+"F35.imprint","IMPRINT",EDGE,{"derivedFrom":subQ0}),1.0]])]});}
            var Q3;
            {var subQ0=sQuery(id+"F35.wireOp",EDGE,"E65");Q3=makeQuery(id+"F35.imprint","IMPRINT",FACE,{"disambiguationData":[TD([[makeQuery(id+"F35.imprint","IMPRINT",EDGE,{"derivedFrom":subQ0}),1.0]])]});}
            extrude(context, id + "F36", {"entities" : qUnion([Q0, Q1, Q2, Q3]), "operationType" : NewBodyOperationType.REMOVE, "oppositeDirection" : true, "depth" : 25 * mm, "offsetDistance" : 25 * mm});
        }
        {
            var Q0;
            {var subQ0=sQuery(id+"F18.wireOp",EDGE,"E44");var subQ2=sQuery(id+"F2.wireOp",EDGE,"E1.left");var subQ3=sQuery(id+"F2.wireOp",EDGE,"E1.top");var subQ5=sQuery(id+"F0.wireOp",EDGE,"E0.left");var subQ6=sQuery(id+"F0.wireOp",EDGE,"E0.bottom");var subQ7=sQuery(id+"F20.wireOp",EDGE,"E46");var subQ8=makeQuery(id+"F21.opExtrude","SWEPT_FACE",FACE,{"disambiguationData":[OSD([subQ7])]});var subQ9=makeQuery(id+"F21.opExtrude","CAP_FACE",FACE,{"disambiguationData":[OSD([subQ6,subQ5,sQuery(id+"F0.wireOp",EDGE,"E0.right"),subQ3,subQ2,subQ7,sQuery(id+"F20.wireOp",EDGE,"E47")])],"isStart":false});Q0=makeQuery(id+"F21.boolean.opBoolean","COPY",EDGE,{"disambiguationData":[topologyDisambiguationEdgeConnected([subQ8,subQ9]),TD([makeQuery(id+"F19.boolean.opBoolean","COPY",FACE,{"derivedFrom":makeQuery(id+"F19.opExtrude","SWEPT_FACE",FACE,{"disambiguationData":[OSD([subQ0])]})})])],"derivedFrom":makeQuery(id+"F21.opExtrude","CAP_EDGE",EDGE,{"disambiguationData":[OSD([subQ7])],"isStart":false})});}
            var Q1;
            {var subQ0=sQuery(id+"F18.wireOp",EDGE,"E45");var subQ3=sQuery(id+"F2.wireOp",EDGE,"E1.left");var subQ4=sQuery(id+"F2.wireOp",EDGE,"E1.top");var subQ5=sQuery(id+"F0.wireOp",EDGE,"E0.left");var subQ6=sQuery(id+"F0.wireOp",EDGE,"E0.bottom");var subQ8=sQuery(id+"F0.wireOp",EDGE,"E0.right");var subQ9=sQuery(id+"F20.wireOp",EDGE,"E46");var subQ10=makeQuery(id+"F21.opExtrude","SWEPT_FACE",FACE,{"disambiguationData":[OSD([subQ9])]});var subQ11=makeQuery(id+"F21.opExtrude","CAP_FACE",FACE,{"disambiguationData":[OSD([subQ6,subQ5,subQ8,subQ4,subQ3,subQ9,sQuery(id+"F20.wireOp",EDGE,"E47")])],"isStart":false});Q1=makeQuery(id+"F21.boolean.opBoolean","COPY",EDGE,{"disambiguationData":[topologyDisambiguationEdgeConnected([subQ10,subQ11]),TD([makeQuery(id+"F19.boolean.opBoolean","COPY",FACE,{"derivedFrom":makeQuery(id+"F19.opExtrude","SWEPT_FACE",FACE,{"disambiguationData":[OSD([subQ0])]})})])],"derivedFrom":makeQuery(id+"F21.opExtrude","CAP_EDGE",EDGE,{"disambiguationData":[OSD([subQ9])],"isStart":false})});}
            var Q2;
            {var subQ0=sQuery(id+"F16.wireOp",EDGE,"E42");var subQ2=sQuery(id+"F0.wireOp",EDGE,"E0.left");var subQ5=sQuery(id+"F0.wireOp",EDGE,"E0.right");var subQ6=sQuery(id+"F0.wireOp",EDGE,"E0.bottom");var subQ7=sQuery(id+"F2.wireOp",EDGE,"E2.left");var subQ8=sQuery(id+"F2.wireOp",EDGE,"E2.top");var subQ9=sQuery(id+"F20.wireOp",EDGE,"E48");var subQ10=makeQuery(id+"F21.opExtrude","CAP_FACE",FACE,{"disambiguationData":[OSD([subQ6,subQ2,subQ5,subQ8,subQ7,subQ9,sQuery(id+"F20.wireOp",EDGE,"E49")])],"isStart":false});var subQ11=makeQuery(id+"F21.opExtrude","SWEPT_FACE",FACE,{"disambiguationData":[OSD([subQ9])]});Q2=makeQuery(id+"F21.boolean.opBoolean","COPY",EDGE,{"disambiguationData":[topologyDisambiguationEdgeConnected([subQ11,subQ10]),TD([makeQuery(id+"F17.boolean.opBoolean","COPY",FACE,{"derivedFrom":makeQuery(id+"F17.opExtrude","SWEPT_FACE",FACE,{"disambiguationData":[OSD([subQ0])]})})])],"derivedFrom":makeQuery(id+"F21.opExtrude","CAP_EDGE",EDGE,{"disambiguationData":[OSD([subQ9])],"isStart":false})});}
            var Q3;
            {var subQ0=sQuery(id+"F16.wireOp",EDGE,"E43");var subQ3=sQuery(id+"F2.wireOp",EDGE,"E2.left");var subQ4=sQuery(id+"F2.wireOp",EDGE,"E2.top");var subQ5=sQuery(id+"F0.wireOp",EDGE,"E0.right");var subQ6=sQuery(id+"F0.wireOp",EDGE,"E0.bottom");var subQ7=sQuery(id+"F20.wireOp",EDGE,"E48");var subQ8=makeQuery(id+"F21.opExtrude","CAP_FACE",FACE,{"disambiguationData":[OSD([subQ6,sQuery(id+"F0.wireOp",EDGE,"E0.left"),subQ5,subQ4,subQ3,subQ7,sQuery(id+"F20.wireOp",EDGE,"E49")])],"isStart":false});var subQ9=makeQuery(id+"F21.opExtrude","SWEPT_FACE",FACE,{"disambiguationData":[OSD([subQ7])]});Q3=makeQuery(id+"F21.boolean.opBoolean","COPY",EDGE,{"disambiguationData":[topologyDisambiguationEdgeConnected([subQ9,subQ8]),TD([makeQuery(id+"F17.boolean.opBoolean","COPY",FACE,{"derivedFrom":makeQuery(id+"F17.opExtrude","SWEPT_FACE",FACE,{"disambiguationData":[OSD([subQ0])]})})])],"derivedFrom":makeQuery(id+"F21.opExtrude","CAP_EDGE",EDGE,{"disambiguationData":[OSD([subQ7])],"isStart":false})});}
            var Q4;
            Q4=makeQuery(id+"F21.boolean.opBoolean","COPY",EDGE,{"derivedFrom":makeQuery(id+"F21.opExtrude","CAP_EDGE",EDGE,{"disambiguationData":[OSD([sQuery(id+"F20.wireOp",EDGE,"E47")])],"isStart":false})});
            var Q5;
            Q5=makeQuery(id+"F21.boolean.opBoolean","COPY",EDGE,{"derivedFrom":makeQuery(id+"F21.opExtrude","CAP_EDGE",EDGE,{"disambiguationData":[OSD([sQuery(id+"F20.wireOp",EDGE,"E49")])],"isStart":false})});
            fillet(context, id + "F37", {"entities" : qUnion([Q0, Q1, Q2, Q3, Q4, Q5]), "radius" : 5 * mm, "tangentPropagation" : true, "allowEdgeOverflow" : false});
        }
        {
            var Q0;
            Q0=makeQuery(id+"F36.boolean.opBoolean","INTERSECT",EDGE,{"derivedFrom":[makeQuery(id+"F17.boolean.opBoolean","COPY",FACE,{"derivedFrom":makeQuery(id+"F17.opExtrude","CAP_FACE",FACE,{"disambiguationData":[OSD([sQuery(id+"F0.wireOp",EDGE,"E0.bottom"),sQuery(id+"F0.wireOp",EDGE,"E0.right"),sQuery(id+"F2.wireOp",EDGE,"E2.top"),sQuery(id+"F2.wireOp",EDGE,"E2.left"),sQuery(id+"F4.wireOp",EDGE,"E3.bottom"),sQuery(id+"F4.wireOp",EDGE,"E3.top"),sQuery(id+"F4.wireOp",EDGE,"E3.left"),sQuery(id+"F16.wireOp",EDGE,"E42"),sQuery(id+"F16.wireOp",EDGE,"E43")])],"isStart":false})}),makeQuery(id+"F36.opExtrude","SWEPT_FACE",FACE,{"disambiguationData":[OSD([sQuery(id+"F35.wireOp",EDGE,"E64")])]})]});
            var Q1;
            {var subQ0=sQuery(id+"F4.wireOp",EDGE,"E3.left");var subQ2=sQuery(id+"F4.wireOp",EDGE,"E3.bottom");var subQ3=sQuery(id+"F2.wireOp",EDGE,"E2.left");var subQ4=sQuery(id+"F0.wireOp",EDGE,"E0.right");var subQ6=sQuery(id+"F0.wireOp",EDGE,"E0.bottom");var subQ7=sQuery(id+"F2.wireOp",EDGE,"E2.top");var subQ11=sQuery(id+"F35.wireOp",EDGE,"E64");Q1=makeQuery(id+"F36.boolean.opBoolean","COPY",EDGE,{"disambiguationData":[topologyDisambiguationEdgeConnected([makeQuery(id+"F22.opExtrude","SWEPT_FACE",FACE,{"disambiguationData":[OSD([subQ6,subQ4,subQ7,subQ3]),TDD([makeQuery(id+"F17.boolean.opBoolean","SPLIT",EDGE,{"disambiguationData":[TD([makeQuery(id+"F17.opExtrude","SWEPT_FACE",FACE,{"disambiguationData":[OSD([sQuery(id+"F16.wireOp",EDGE,"E42")])]})])],"derivedFrom":makeQuery(id+"F14.opExtrude","CAP_EDGE",EDGE,{"disambiguationData":[OSD([subQ6,subQ4,subQ7,subQ3])],"isStart":false})})])]})])],"derivedFrom":makeQuery(id+"F36.opExtrude","SWEPT_EDGE",EDGE,{"disambiguationData":[OSD([subQ7,subQ3,subQ2,subQ0,subQ11])]})});}
            var Q2;
            {var subQ0=sQuery(id+"F4.wireOp",EDGE,"E3.left");var subQ1=sQuery(id+"F4.wireOp",EDGE,"E3.bottom");var subQ2=sQuery(id+"F2.wireOp",EDGE,"E2.left");var subQ3=sQuery(id+"F0.wireOp",EDGE,"E0.right");var subQ5=sQuery(id+"F0.wireOp",EDGE,"E0.bottom");var subQ6=sQuery(id+"F2.wireOp",EDGE,"E2.top");var subQ8=sQuery(id+"F35.wireOp",EDGE,"E64");Q2=makeQuery(id+"F36.boolean.opBoolean","COPY",EDGE,{"disambiguationData":[topologyDisambiguationEdgeConnected([makeQuery(id+"F22.opExtrude","SWEPT_FACE",FACE,{"disambiguationData":[OSD([subQ5,subQ3,subQ6,subQ2]),TDD([makeQuery(id+"F17.boolean.opBoolean","SPLIT",EDGE,{"disambiguationData":[TD([makeQuery(id+"F17.opExtrude","SWEPT_FACE",FACE,{"disambiguationData":[OSD([sQuery(id+"F16.wireOp",EDGE,"E43")])]})])],"derivedFrom":makeQuery(id+"F14.opExtrude","CAP_EDGE",EDGE,{"disambiguationData":[OSD([subQ5,subQ3,subQ6,subQ2])],"isStart":false})})])]})])],"derivedFrom":makeQuery(id+"F36.opExtrude","SWEPT_EDGE",EDGE,{"disambiguationData":[OSD([subQ6,subQ2,subQ1,subQ0,subQ8])]})});}
            var Q3;
            Q3=makeQuery(id+"F34.boolean.opBoolean","INTERSECT",EDGE,{"derivedFrom":[makeQuery(id+"F19.boolean.opBoolean","COPY",FACE,{"derivedFrom":makeQuery(id+"F19.opExtrude","CAP_FACE",FACE,{"disambiguationData":[OSD([sQuery(id+"F0.wireOp",EDGE,"E0.bottom"),sQuery(id+"F0.wireOp",EDGE,"E0.left"),sQuery(id+"F2.wireOp",EDGE,"E1.top"),sQuery(id+"F2.wireOp",EDGE,"E1.left"),sQuery(id+"F4.wireOp",EDGE,"E4.bottom"),sQuery(id+"F4.wireOp",EDGE,"E4.top"),sQuery(id+"F4.wireOp",EDGE,"E4.left"),sQuery(id+"F18.wireOp",EDGE,"E44"),sQuery(id+"F18.wireOp",EDGE,"E45")])],"isStart":false})}),makeQuery(id+"F34.opExtrude","SWEPT_FACE",FACE,{"disambiguationData":[OSD([sQuery(id+"F33.wireOp",EDGE,"E60")])]})]});
            var Q4;
            {var subQ0=sQuery(id+"F4.wireOp",EDGE,"E4.left");var subQ1=sQuery(id+"F4.wireOp",EDGE,"E4.bottom");var subQ2=sQuery(id+"F2.wireOp",EDGE,"E1.left");var subQ3=sQuery(id+"F0.wireOp",EDGE,"E0.left");var subQ6=sQuery(id+"F0.wireOp",EDGE,"E0.bottom");var subQ7=sQuery(id+"F2.wireOp",EDGE,"E1.top");var subQ8=sQuery(id+"F33.wireOp",EDGE,"E60");Q4=makeQuery(id+"F34.boolean.opBoolean","COPY",EDGE,{"disambiguationData":[topologyDisambiguationEdgeConnected([makeQuery(id+"F22.opExtrude","SWEPT_FACE",FACE,{"disambiguationData":[OSD([subQ6,subQ3,subQ7,subQ2]),TDD([makeQuery(id+"F19.boolean.opBoolean","SPLIT",EDGE,{"disambiguationData":[TD([makeQuery(id+"F19.opExtrude","SWEPT_FACE",FACE,{"disambiguationData":[OSD([sQuery(id+"F18.wireOp",EDGE,"E44")])]})])],"derivedFrom":makeQuery(id+"F15.opExtrude","CAP_EDGE",EDGE,{"disambiguationData":[OSD([subQ6,subQ3,subQ7,subQ2])],"isStart":false})})])]})])],"derivedFrom":makeQuery(id+"F34.opExtrude","SWEPT_EDGE",EDGE,{"disambiguationData":[OSD([subQ7,subQ2,subQ1,subQ0,subQ8])]})});}
            var Q5;
            {var subQ0=sQuery(id+"F4.wireOp",EDGE,"E4.left");var subQ2=sQuery(id+"F4.wireOp",EDGE,"E4.bottom");var subQ3=sQuery(id+"F2.wireOp",EDGE,"E1.left");var subQ4=sQuery(id+"F0.wireOp",EDGE,"E0.left");var subQ8=sQuery(id+"F0.wireOp",EDGE,"E0.bottom");var subQ10=sQuery(id+"F2.wireOp",EDGE,"E1.top");var subQ11=sQuery(id+"F33.wireOp",EDGE,"E60");Q5=makeQuery(id+"F34.boolean.opBoolean","COPY",EDGE,{"disambiguationData":[topologyDisambiguationEdgeConnected([makeQuery(id+"F22.opExtrude","SWEPT_FACE",FACE,{"disambiguationData":[OSD([subQ8,subQ4,subQ10,subQ3]),TDD([makeQuery(id+"F19.boolean.opBoolean","SPLIT",EDGE,{"disambiguationData":[TD([makeQuery(id+"F19.opExtrude","SWEPT_FACE",FACE,{"disambiguationData":[OSD([sQuery(id+"F18.wireOp",EDGE,"E45")])]})])],"derivedFrom":makeQuery(id+"F15.opExtrude","CAP_EDGE",EDGE,{"disambiguationData":[OSD([subQ8,subQ4,subQ10,subQ3])],"isStart":false})})])]})])],"derivedFrom":makeQuery(id+"F34.opExtrude","SWEPT_EDGE",EDGE,{"disambiguationData":[OSD([subQ10,subQ3,subQ2,subQ0,subQ11])]})});}
            chamfer(context, id + "F38", {"entities" : qUnion([Q0, Q1, Q2, Q3, Q4, Q5]), "width" : 5 * mm, "tangentPropagation" : true});
        }
        {
            var Q0;
            {var subQ0=sQuery(id+"F4.wireOp",EDGE,"E3.left");var subQ1=sQuery(id+"F4.wireOp",EDGE,"E3.bottom");var subQ2=sQuery(id+"F2.wireOp",EDGE,"E2.left");var subQ3=sQuery(id+"F2.wireOp",EDGE,"E2.top");Q0=makeQuery(id+"F25.boolean.opBoolean","MERGE",FACE,{"derivedFrom":[makeQuery(id+"F22.boolean.opBoolean","MERGE",FACE,{"derivedFrom":[makeQuery(id+"F14.boolean.opBoolean","MERGE",FACE,{"derivedFrom":[makeQuery(id+"F12.opExtrude","CAP_FACE",FACE,{"disambiguationData":[OSD([sQuery(id+"F2.wireOp",EDGE,"E2.bottom"),subQ3,subQ2,sQuery(id+"F2.wireOp",EDGE,"E2.right"),subQ1])],"isStart":false}),makeQuery(id+"F14.opExtrude","SWEPT_FACE",FACE,{"disambiguationData":[OSD([subQ2,subQ1,subQ0])]})]}),makeQuery(id+"F22.opExtrude","SWEPT_FACE",FACE,{"disambiguationData":[OSD([subQ3,subQ2])]})]}),makeQuery(id+"F25.opExtrude","SWEPT_FACE",FACE,{"disambiguationData":[OSD([subQ3,subQ2,subQ1,subQ0])]})]});}
            var sketch = newSketch(context, id + "F39", { "sketchPlane" : qUnion([Q0])});
            skLineSegment(sketch, "E66", {"start": v(98.75, 70) * mm, "end": v(118.25, 70) * mm});
            skLineSegment(sketch, "E67", {"start": v(98.75, 70) * mm, "end": v(-18.85, 70) * mm});
            skLineSegment(sketch, "E68", {"start": v(-18.85, 70) * mm, "end": v(-18.85, 185.54) * mm});
            skLineSegment(sketch, "E69", {"start": v(-18.85, 185.54) * mm, "end": v(118.25, 185.54) * mm});
            skLineSegment(sketch, "E70", {"start": v(118.25, 185.54) * mm, "end": v(118.25, 70) * mm});
            skSolve(sketch);
        }
        {
            var Q0;
            {var subQ28=sQuery(id+"F39.wireOp",EDGE,"E68");Q0=makeQuery(id+"F39.imprint","IMPRINT",FACE,{"disambiguationData":[TD([[makeQuery(id+"F39.imprint","IMPRINT",EDGE,{"derivedFrom":subQ28}),-1.0]])]});}
            var Q1;
            {var subQ22=sQuery(id+"F39.wireOp",EDGE,"E66");Q1=makeQuery(id+"F39.imprint","IMPRINT",FACE,{"disambiguationData":[TD([[makeQuery(id+"F39.imprint","IMPRINT",EDGE,{"derivedFrom":subQ22}),1.0]])]});}
            extrude(context, id + "F40", {"entities" : qUnion([Q0, Q1]), "operationType" : NewBodyOperationType.REMOVE, "oppositeDirection" : true, "depth" : 35 * mm, "offsetDistance" : 25 * mm});
        }
    });
